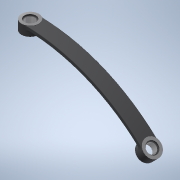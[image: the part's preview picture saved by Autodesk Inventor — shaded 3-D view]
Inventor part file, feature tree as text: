
AUTODESK INVENTOR PART (.ipt)
format: ipt  version: 2020.1 (Build 241239000, 239)  size: 292,352 bytes
history: native  units: mm
features: hole x6, sketch x5, plane x3, extrude x3, fillet x3, other x2, thicken_offset x1, revolve x1
ambient origin geometry x8: Origin, YZ Plane, XZ Plane, XY Plane, X Axis, Y Axis, Z Axis, Center Point
bodies: Solid1 (feature_tree)
feature tree (24):
  sketch  "3D Sketch1"
  plane  "Work Plane1"
  sketch  "Sketch2"  dims[d2=180.0mm d4=180.0mm]
  thicken_offset  "Thicken1"
  extrude  "Extrusion1"  TaperAngle=180.0deg  [1 undecoded]
  plane  "Work Plane2"
  extrude  "Extrusion2"  Depth=180.0mm
  plane  "Work Plane3"
  extrude  "Extrusion3"  Depth=4.0mm
  hole  "Hole1"  [1 undecoded]
  hole  "Hole2"  [1 undecoded]
  fillet  "Fillet1"  Radius=18.0mm
  fillet  "Fillet2"  Radius=10.0mm
  fillet  "Fillet3"  Radius=10.0mm
  hole  "Hole4"  [1 undecoded]
  hole  "Hole5"  [1 undecoded]
  hole  "Hole6"  [1 undecoded]
  hole  "Hole7"  [1 undecoded]
  sketch  "Sketch1"  dims[d0=180.0mm d1=180.0deg]
  other  "Srf1"
  sketch  "Sketch3"  dims[d5=16.0mm d6=4.0mm d7=8.0mm]
  sketch  "Sketch4"  dims[d8=10.0mm d9=0.0mm d10=18.0mm d11=10.0mm d12=0.0mm d13=18.0mm d14=10.0mm d15=0.0mm d16=10.0mm d17=10.0mm d18=10.0mm d19=6.0mm d20=4.0mm d21=2.0mm d22=90.0deg d23=8.0mm d24=20.594885mm d25=10.0mm d26=10.0mm d27=10.0mm d28=6.0mm d29=4.0mm d30=2.0mm d31=90.0deg d32=8.0mm d33=20.594885mm d34=1.0mm d35=10.0mm d36=0.7mm d52=45.0deg d53=10.0mm d54=10.0mm d55=12.0mm d56=6.0mm d57=4.0mm d58=2.0mm d59=90.0deg d60=1.5mm d61=0.0mm d62=10.0mm d63=10.0mm d64=12.0mm d65=6.0mm d66=4.0mm d67=2.0mm d68=90.0deg d69=1.5mm d70=0.0mm d71=10.0mm d72=10.0mm d73=12.0mm d74=6.0mm d75=4.0mm d76=2.0mm d77=90.0deg d78=1.5mm d79=0.0mm d80=10.0mm d81=10.0mm d82=12.0mm d83=6.0mm d84=4.0mm d85=2.0mm d86=90.0deg d87=1.5mm d88=0.0mm]
  revolve  "RevolutionSrf1"  Angle=45.0deg
  other  "3D Intersection1"
note: 7 required parameter values undecoded (feature->parameter linkage not recoverable at this tier; creation-order binding heuristic only, values carry confidence <= 0.55)
